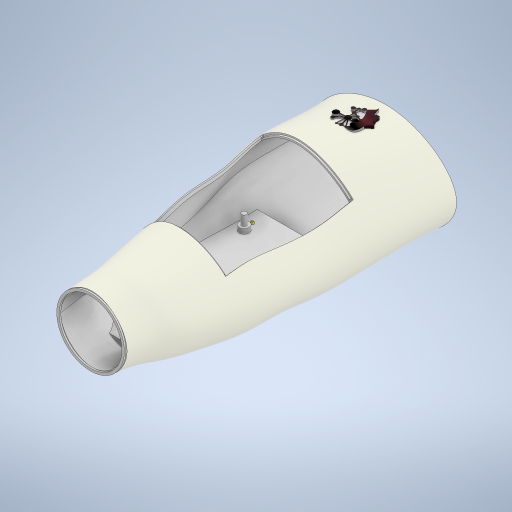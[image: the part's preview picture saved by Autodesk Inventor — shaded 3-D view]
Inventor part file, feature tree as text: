
AUTODESK INVENTOR PART (.ipt)
format: ipt  version: 2024 (Build 280153000, 153)  size: 1,447,936 bytes
history: native  units: mm
features: other x24, extrude x10, sketch x6, projected_geometry x6, move_body x2, direct_edit x1
ambient origin geometry x8: Origin, YZ Plane, XZ Plane, XY Plane, X Axis, Y Axis, Z Axis, Center Point
bodies: Body1 (feature_tree), Body2 (feature_tree), Body3 (feature_tree), Body4 (feature_tree)
feature tree (49):
  other  "Sólido6"
  other  "Antebrazo medidas"
  other  "Plano elipse"
  other  "Plano circulo"
  other  "Union muñeca (circulo)"
  other  "Entrada Antebrazo"
  other  "Forma1"
  other  "Plano de railes"
  sketch  "Boceto10"  dims[d0=180.0mm d1=43.0mm]
  other  "Coser superficie6"
  other  "Suprimir cara7"
  other  "Engrosado3"
  extrude  "Extrusión3"  Depth=43.0mm
  other  "Plano desfasado"
  extrude  "Extrusión6"  Depth=43.0mm
  other  "Plano abajo"
  other  "Rectangulo abajo"
  other  "Plano bases"
  extrude  "cols"  Depth=41.8mm
  other  "Logotipo"
  extrude  "Extrusión9"  Depth=2.0mm
  extrude  "Extrusión10"  [1 undecoded]
  other  "dirLogo"
  direct_edit  "Direct Edit6"
  extrude  "col2INO"  Depth=54.0mm
  extrude  "Extrusion12"  Depth=35.0mm TaperAngle=0.0deg
  extrude  "Extrusion13"  Depth=75.0mm
  other  "Lip1"
  extrude  "Extrusion14"  [1 undecoded]
  extrude  "Extrusion15"  Depth=75.5mm
  sketch  "Boceto12"  dims[d2=20.9mm d8=43.0mm]
  other  "Corte"
  other  "Puntos Base"
  sketch  "Boceto18"  dims[d9=20.9mm d14=41.8mm]
  sketch  "Boceto19"  dims[d15=30.0mm d54=2.0mm]
  projected_geometry  "Projected Loop1"
  projected_geometry  "Projected Loop2"
  sketch  "Sketch24"  dims[d55=0.0mm d56=0.0mm d57=-40.0mm]
  sketch  "Sketch26"  dims[d58=75.5mm d59=54.0mm d64=35.0mm d65=0.0mm d68=75.0mm d71=-19.0mm d72=75.5mm d73=0.043mm d76=10.0mm d77=0.0mm d78=-33.0mm d79=2.148mm d80=0.0mm d81=70.0mm d82=110.0mm d83=10.0mm d84=0.0mm d94=0.0mm d95=0.0mm d96=-1.75mm d102=5.08mm d103=6.0mm d105=65.0mm d106=0.0mm d107=0.0mm d108=-4.2mm d110=52.07mm d111=27.94mm d112=15.24mm d113=50.8mm d114=17.8mm d118=3.0mm d119=9.0mm d120=0.0mm d122=2.0mm d123=0.0mm d124=1.5mm d125=1.0mm d126=0.0mm d128=1.0mm d129=1.0mm d130=0.0mm d131=0.0mm d132=0.0mm d133=0.0mm d134=20.0mm d135=10.0mm d136=3.0mm d137=0.0mm d138=6.0mm d139=6.0mm d140=6.0mm d141=6.0mm d142=27.94mm d143=50.8mm d144=52.07mm d145=15.24mm d146=63.0mm d147=19.9898mm d148=8.0mm d149=8.0mm d150=8.0mm d151=8.0mm d152=8.0mm d153=8.0mm d154=35.0mm d155=40.0mm d156=50.0126mm d157=40.0mm d158=50.013mm d159=17.0mm d160=0.0mm d161=6.995mm d38=0.5mm d39=0.872665mm d40=0.5mm d41=0.872665mm d60=0.5mm d61=0.872665mm d74=0.5mm d75=0.872665mm]
  other  "Sup1"
  other  "Sup12"
  other  "Sup13"
  projected_geometry  "Project Cut Edges1"
  move_body  "Move4"
  projected_geometry  "Project Cut Edges2"
  move_body  "Move6"
  projected_geometry  "Project Cut Edges3"
  projected_geometry  "Project Cut Edges4"
  other  "Finish1"
note: 2 required parameter values undecoded (feature->parameter linkage not recoverable at this tier; creation-order binding heuristic only, values carry confidence <= 0.55)
